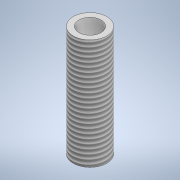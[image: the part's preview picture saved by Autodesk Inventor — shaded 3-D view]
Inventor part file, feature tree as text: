
AUTODESK INVENTOR PART (.ipt)
format: ipt  version: 2022 (Build 260153000, 153)  size: 114,176 bytes
history: native  units: mm
features: sketch x2, other x1, extrude x1, thread x1, hole x1
ambient origin geometry x8: Origin, YZ Plane, XZ Plane, XY Plane, X Axis, Y Axis, Z Axis, Center Point
bodies: Body1 (feature_tree)
feature tree (6):
  other  "Sólido1"
  extrude  "Extrusión1"  Depth=50.0mm TaperAngle=0.0deg
  thread  "Rosca1"  [1 undecoded]
  hole  "Agujero1"  [1 undecoded]
  sketch  "Boceto1"  dims[d0=15.164mm d1=50.0mm d2=0.0mm d3=45.0mm d4=0.0mm]
  sketch  "Boceto2"  dims[d5=10.0mm d6=10.0mm d7=4.0mm d8=2.0mm d9=90.0deg d10=8.0mm d11=20.594885mm]
note: 2 required parameter values undecoded (feature->parameter linkage not recoverable at this tier; creation-order binding heuristic only, values carry confidence <= 0.55)
